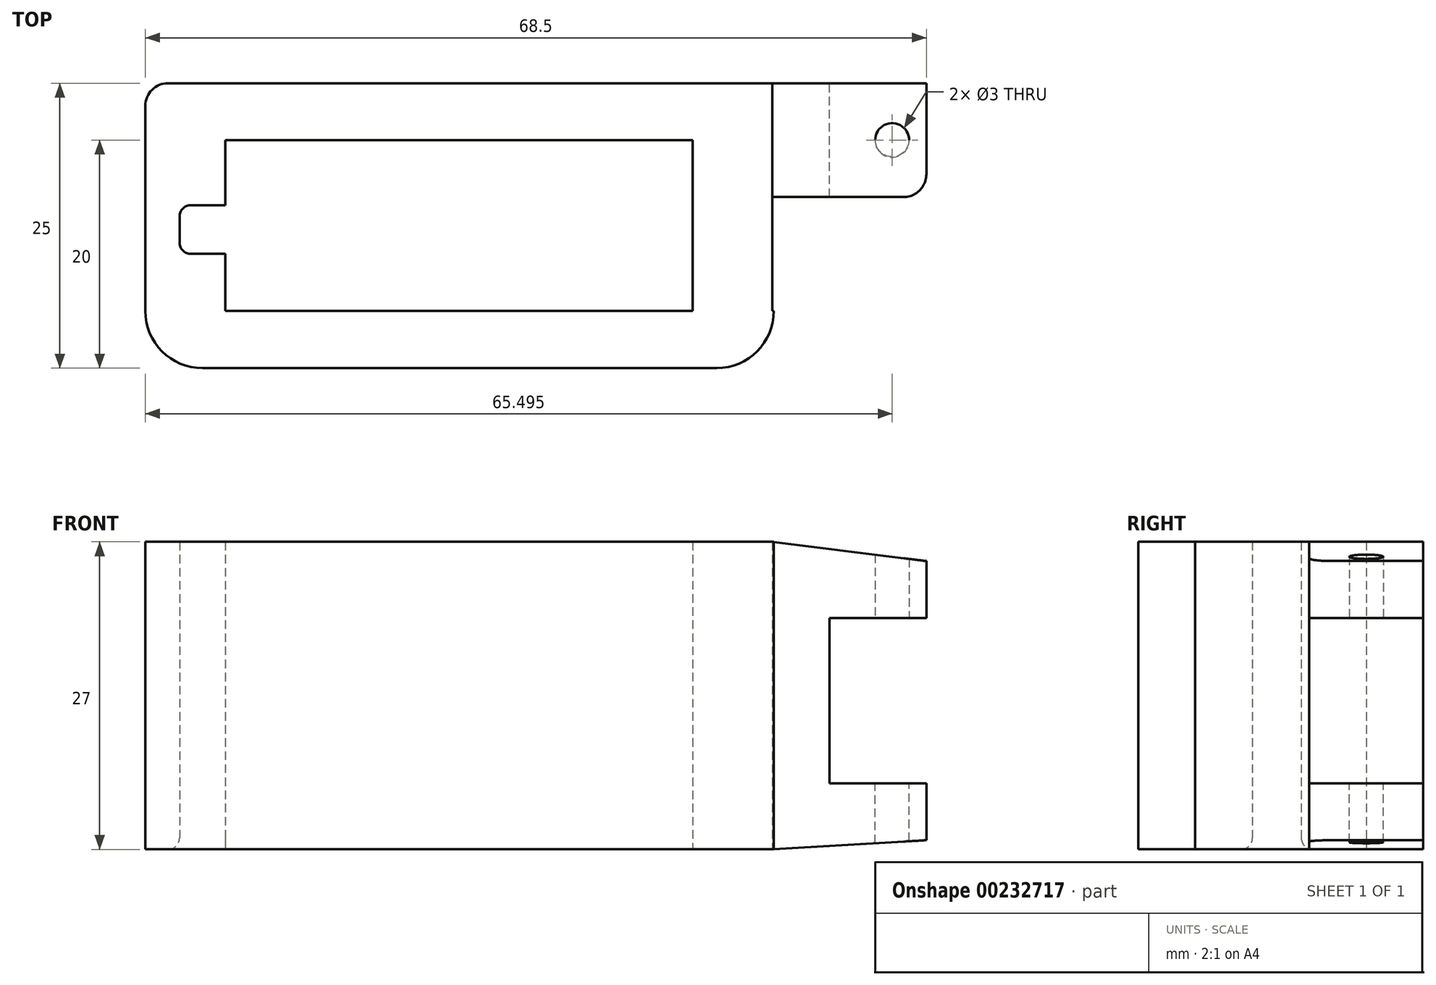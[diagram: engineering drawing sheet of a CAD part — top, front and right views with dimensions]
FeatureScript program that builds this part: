
annotation { "Feature Type Name" : "Feature", "Feature Type Description" : "" }
export const myFeature = defineFeature(function(context is Context, id is Id, definition is map)
    precondition{}
    {
        {
            var Q0;
            Q0=qCreatedBy(makeId("Front.planeOp"),FACE);
            var sketch = newSketch(context, id + "F0", { "sketchPlane" : qUnion([Q0])});
            skLineSegment(sketch, "E0.bottom", {"start": v(-27.61, 13.31) * mm, "end": v(27.39, 13.31) * mm});
            skLineSegment(sketch, "E0.top", {"start": v(-27.61, -13.69) * mm, "end": v(27.39, -13.69) * mm});
            skLineSegment(sketch, "E0.left", {"start": v(-27.61, 13.31) * mm, "end": v(-27.61, -13.69) * mm});
            skLineSegment(sketch, "E0.right", {"start": v(27.39, 13.31) * mm, "end": v(27.39, -13.69) * mm});
            skLineSegment(sketch, "E1", {"start": v(27.39, 13.31) * mm, "end": v(40.89, 11.62) * mm});
            skLineSegment(sketch, "E2", {"start": v(40.89, 11.62) * mm, "end": v(40.89, 6.62) * mm});
            skLineSegment(sketch, "E3", {"start": v(40.89, 6.62) * mm, "end": v(32.39, 6.62) * mm});
            skLineSegment(sketch, "E4", {"start": v(32.39, 6.62) * mm, "end": v(32.39, -7.88) * mm});
            skLineSegment(sketch, "E5", {"start": v(32.39, -7.88) * mm, "end": v(40.89, -7.88) * mm});
            skLineSegment(sketch, "E6", {"start": v(40.89, -7.88) * mm, "end": v(40.89, -12.88) * mm});
            skLineSegment(sketch, "E7", {"start": v(40.89, -12.88) * mm, "end": v(27.39, -13.69) * mm});
            skLineSegment(sketch, "E8", {"start": v(20.39, 13.31) * mm, "end": v(20.39, -13.69) * mm});
            skLineSegment(sketch, "E9", {"start": v(-20.61, 13.31) * mm, "end": v(-20.61, -13.69) * mm});
            skSolve(sketch);
        }
        {
            var Q0;
            {var subQ0=sQuery(id+"F0.wireOp",EDGE,"E8");Q0=makeQuery(id+"F0.imprint","IMPRINT",FACE,{"disambiguationData":[TD([[makeQuery(id+"F0.imprint","IMPRINT",EDGE,{"derivedFrom":subQ0}),-1.0]])]});}
            extrude(context, id + "F1", {"entities" : qUnion([Q0]), "depth" : 5 * mm});
        }
        {
            var Q0;
            {var subQ0=sQuery(id+"F0.wireOp",EDGE,"E0.right");Q0=makeQuery(id+"F0.imprint","IMPRINT",FACE,{"disambiguationData":[TD([[makeQuery(id+"F0.imprint","IMPRINT",EDGE,{"derivedFrom":subQ0}),-1.0]])]});}
            extrude(context, id + "F2", {"entities" : qUnion([Q0]), "operationType" : NewBodyOperationType.ADD, "depth" : 20 * mm});
        }
        {
            var Q0;
            {var subQ0=sQuery(id+"F0.wireOp",EDGE,"E0.left");Q0=makeQuery(id+"F0.imprint","IMPRINT",FACE,{"disambiguationData":[TD([[makeQuery(id+"F0.imprint","IMPRINT",EDGE,{"derivedFrom":subQ0}),1.0]])]});}
            extrude(context, id + "F3", {"entities" : qUnion([Q0]), "operationType" : NewBodyOperationType.ADD, "depth" : 20 * mm});
        }
        {
            var Q0;
            Q0=makeQuery(id+"F0.imprint","IMPRINT",FACE,{"disambiguationData":[TD([[makeQuery(id+"F0.imprint","IMPRINT",EDGE,{"derivedFrom":sQuery(id+"F0.wireOp",EDGE,"E0.right")}),1.0]])]});
            extrude(context, id + "F4", {"entities" : qUnion([Q0]), "operationType" : NewBodyOperationType.ADD, "depth" : 10 * mm});
        }
        {
            var Q0;
            Q0=makeQuery(id+"F4.opExtrude","CAP_EDGE",EDGE,{"disambiguationData":[OSD([sQuery(id+"F0.wireOp",EDGE,"E0.right")])],"isStart":false});
            var Q1;
            Q1=makeQuery(id+"F3.opExtrude","CAP_EDGE",EDGE,{"disambiguationData":[OSD([sQuery(id+"F0.wireOp",EDGE,"E0.left")])],"isStart":true});
            var Q2;
            Q2=makeQuery(id+"F4.opExtrude","CAP_EDGE",EDGE,{"disambiguationData":[OSD([sQuery(id+"F0.wireOp",EDGE,"E6")])],"isStart":false});
            var Q3;
            Q3=makeQuery(id+"F4.opExtrude","CAP_EDGE",EDGE,{"disambiguationData":[OSD([sQuery(id+"F0.wireOp",EDGE,"E2")])],"isStart":false});
            fillet(context, id + "F5", {"entities" : qUnion([Q0, Q1, Q2, Q3]), "radius" : 2 * mm, "tangentPropagation" : true, "allowEdgeOverflow" : false});
        }
        {
            var Q0;
            Q0=makeQuery(id+"F4.opExtrude","SWEPT_FACE",FACE,{"disambiguationData":[OSD([sQuery(id+"F0.wireOp",EDGE,"E5")])]});
            var sketch = newSketch(context, id + "F6", { "sketchPlane" : qUnion([Q0])});
            skPoint(sketch, "E10", {"position": v(37.89, -5) * mm});
            skSolve(sketch);
        }
        {
            var Q0;
            Q0=makeQuery(id+"F4.opExtrude","SWEPT_FACE",FACE,{"disambiguationData":[OSD([sQuery(id+"F0.wireOp",EDGE,"E3")])]});
            var sketch = newSketch(context, id + "F7", { "sketchPlane" : qUnion([Q0])});
            skPoint(sketch, "E11", {"position": v(37.89, 5) * mm});
            skSolve(sketch);
        }
        {
            var Q0;
            Q0=sQuery(id+"F7.wireOp",VERTEX,"E11");
            var Q1;
            Q1=sQuery(id+"F6.wireOp",VERTEX,"E10");
            var Q2;
            Q2=makeQuery(id+"F1.opExtrude","SWEPT_BODY",BODY,{"disambiguationData":[OSD([sQuery(id+"F0.wireOp",EDGE,"E0.bottom"),sQuery(id+"F0.wireOp",EDGE,"E0.top"),sQuery(id+"F0.wireOp",EDGE,"E8"),sQuery(id+"F0.wireOp",EDGE,"E9")])]});
            hole(context, id + "F8", {"style" : HoleStyle.SIMPLE, "endStyle" : HoleEndStyle.BLIND, "holeDiameter" : 3 * mm, "holeDepth" : 12 * mm, "startFromSketch" : true, "locations" : qUnion([Q0, Q1]), "scope" : qUnion([Q2])});
        }
        {
            var Q0;
            Q0=makeQuery(id+"F3.opExtrude","CAP_FACE",FACE,{"disambiguationData":[OSD([sQuery(id+"F0.wireOp",EDGE,"E0.bottom"),sQuery(id+"F0.wireOp",EDGE,"E0.top"),sQuery(id+"F0.wireOp",EDGE,"E0.left"),sQuery(id+"F0.wireOp",EDGE,"E9")])],"isStart":false});
            var sketch = newSketch(context, id + "F9", { "sketchPlane" : qUnion([Q0])});
            skLineSegment(sketch, "E12.bottom", {"start": v(-27.61, 13.31) * mm, "end": v(27.5, 13.31) * mm});
            skLineSegment(sketch, "E12.top", {"start": v(-27.61, -13.69) * mm, "end": v(27.5, -13.69) * mm});
            skLineSegment(sketch, "E12.left", {"start": v(-27.61, 13.31) * mm, "end": v(-27.61, -13.69) * mm});
            skLineSegment(sketch, "E12.right", {"start": v(27.5, 13.31) * mm, "end": v(27.5, -13.69) * mm});
            skSolve(sketch);
        }
        {
            var Q0;
            {var subQ2=sQuery(id+"F9.wireOp",EDGE,"E12.right");Q0=makeQuery(id+"F9.imprint","IMPRINT",FACE,{"disambiguationData":[TD([[makeQuery(id+"F9.imprint","IMPRINT",EDGE,{"derivedFrom":subQ2}),-1.0]])]});}
            var Q1;
            Q1 = qSketchRegion(id + "F9", true);
            extrude(context, id + "F10", {"entities" : qUnion([Q0, Q1]), "operationType" : NewBodyOperationType.ADD, "depth" : 5 * mm});
        }
        {
            var Q0;
            Q0=makeQuery(id+"F10.opExtrude","CAP_EDGE",EDGE,{"disambiguationData":[OSD([sQuery(id+"F9.wireOp",EDGE,"E12.right")])],"isStart":false});
            var Q1;
            Q1=makeQuery(id+"F10.opExtrude","CAP_EDGE",EDGE,{"disambiguationData":[OSD([sQuery(id+"F9.wireOp",EDGE,"E12.left")])],"isStart":false});
            fillet(context, id + "F11", {"entities" : qUnion([Q0, Q1]), "radius" : 5 * mm, "tangentPropagation" : true, "allowEdgeOverflow" : false});
        }
        {
            var Q0;
            Q0=makeQuery(id+"F3.opExtrude","SWEPT_FACE",FACE,{"disambiguationData":[OSD([sQuery(id+"F0.wireOp",EDGE,"E9")])]});
            var sketch = newSketch(context, id + "F12", { "sketchPlane" : qUnion([Q0])});
            skLineSegment(sketch, "E13.bottom", {"start": v(-14.99, 13.31) * mm, "end": v(-10.7, 13.31) * mm});
            skLineSegment(sketch, "E13.top", {"start": v(-14.99, -13.8) * mm, "end": v(-10.7, -13.8) * mm});
            skLineSegment(sketch, "E13.left", {"start": v(-14.99, 13.31) * mm, "end": v(-14.99, -13.8) * mm});
            skLineSegment(sketch, "E13.right", {"start": v(-10.7, 13.31) * mm, "end": v(-10.7, -13.8) * mm});
            skSolve(sketch);
        }
        {
            var Q0;
            Q0 = qSketchRegion(id + "F12", true);
            extrude(context, id + "F13", {"entities" : qUnion([Q0]), "operationType" : NewBodyOperationType.REMOVE, "oppositeDirection" : true, "depth" : 4 * mm});
        }
        {
            var Q0;
            Q0=makeQuery(id+"F13.boolean.opBoolean","COPY",EDGE,{"derivedFrom":makeQuery(id+"F13.opExtrude","CAP_EDGE",EDGE,{"disambiguationData":[OSD([sQuery(id+"F12.wireOp",EDGE,"E13.left")])],"isStart":false})});
            var Q1;
            Q1=makeQuery(id+"F13.boolean.opBoolean","COPY",EDGE,{"derivedFrom":makeQuery(id+"F13.opExtrude","CAP_EDGE",EDGE,{"disambiguationData":[OSD([sQuery(id+"F12.wireOp",EDGE,"E13.right")])],"isStart":false})});
            var Q2;
            Q2=makeQuery(id+"F13.boolean.opBoolean","COPY",EDGE,{"derivedFrom":makeQuery(id+"F13.opExtrude","CAP_EDGE",EDGE,{"disambiguationData":[OSD([sQuery(id+"F12.wireOp",EDGE,"E13.bottom")])],"isStart":false})});
            fillet(context, id + "F14", {"entities" : qUnion([Q0, Q1, Q2]), "radius" : 1 * mm, "tangentPropagation" : true, "allowEdgeOverflow" : false});
        }
        {
            var Q0;
            {var subQ0=sQuery(id+"F0.wireOp",EDGE,"E0.top");Q0=makeQuery(id+"F13.boolean.opBoolean","INTERSECT",EDGE,{"derivedFrom":[makeQuery(id+"F10.boolean.opBoolean","MERGE",FACE,{"derivedFrom":[makeQuery(id+"F3.boolean.opBoolean","MERGE",FACE,{"derivedFrom":[makeQuery(id+"F2.boolean.opBoolean","MERGE",FACE,{"derivedFrom":[makeQuery(id+"F1.opExtrude","SWEPT_FACE",FACE,{"disambiguationData":[OSD([subQ0])]}),makeQuery(id+"F2.opExtrude","SWEPT_FACE",FACE,{"disambiguationData":[OSD([subQ0])]})]}),makeQuery(id+"F3.opExtrude","SWEPT_FACE",FACE,{"disambiguationData":[OSD([subQ0])]})]}),makeQuery(id+"F10.opExtrude","SWEPT_FACE",FACE,{"disambiguationData":[OSD([sQuery(id+"F9.wireOp",EDGE,"E12.top")])]})]}),makeQuery(id+"F13.opExtrude","SWEPT_FACE",FACE,{"disambiguationData":[OSD([sQuery(id+"F12.wireOp",EDGE,"E13.left")])]})]});}
            fillet(context, id + "F15", {"entities" : qUnion([Q0]), "radius" : 1 * mm, "tangentPropagation" : true, "allowEdgeOverflow" : false});
        }
    });
